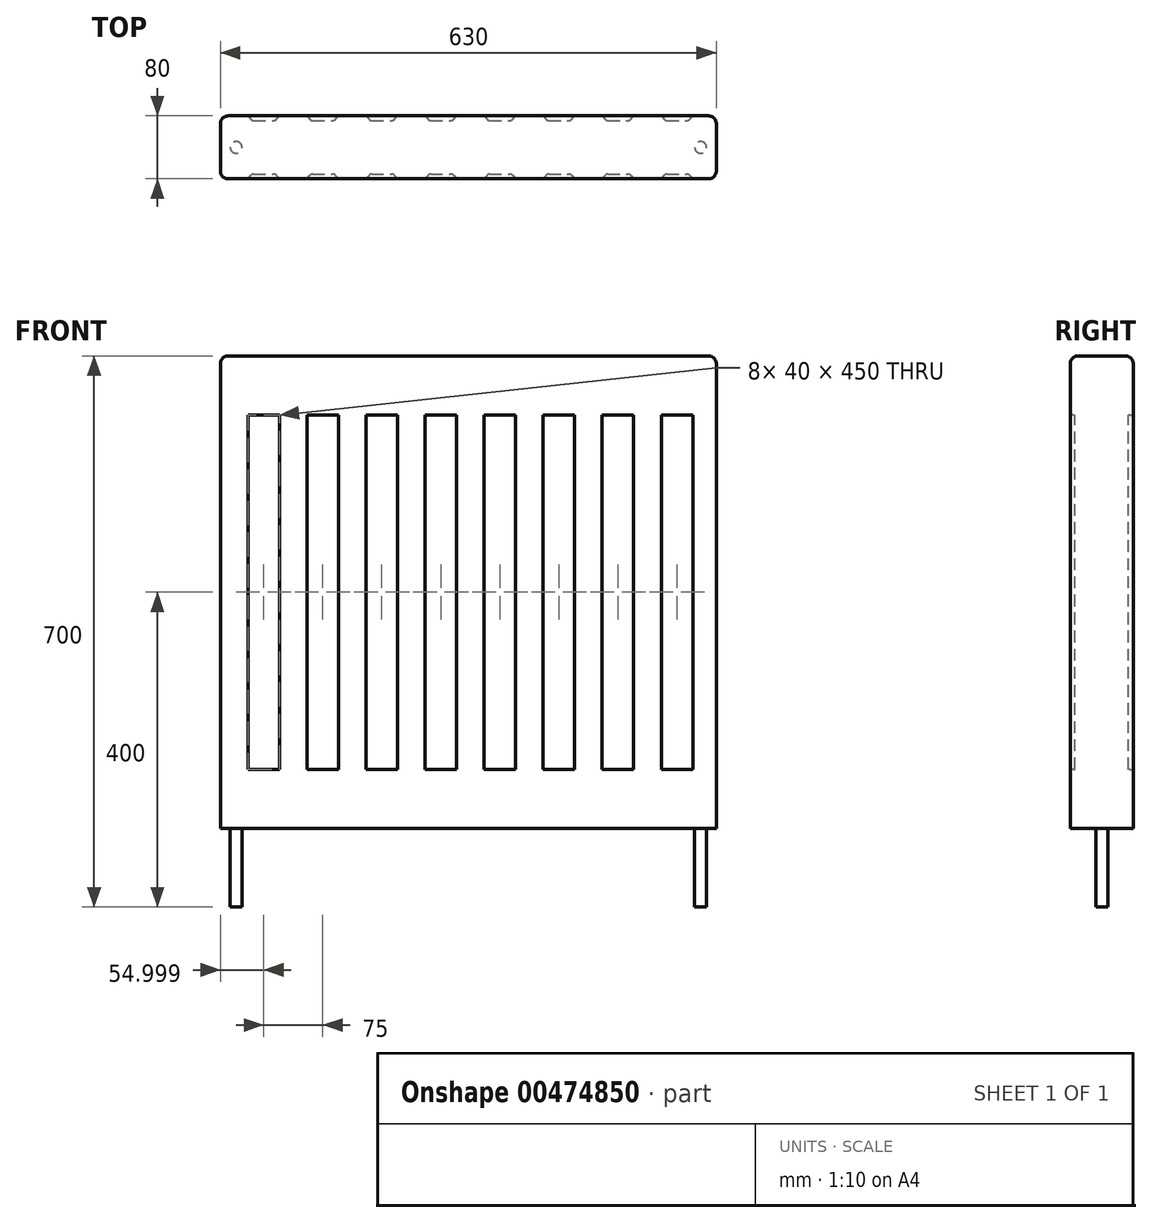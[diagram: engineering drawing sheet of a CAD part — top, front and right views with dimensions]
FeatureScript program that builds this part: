
annotation { "Feature Type Name" : "Feature", "Feature Type Description" : "" }
export const myFeature = defineFeature(function(context is Context, id is Id, definition is map)
    precondition{}
    {
        {
            var Q0;
            Q0=qCreatedBy(makeId("Top.planeOp"),FACE);
            var sketch = newSketch(context, id + "F0", { "sketchPlane" : qUnion([Q0])});
            skLineSegment(sketch, "E0.bottom", {"start": v(-345.66, -18.68) * mm, "end": v(284.34, -18.68) * mm});
            skLineSegment(sketch, "E0.top", {"start": v(-345.66, -98.68) * mm, "end": v(284.34, -98.68) * mm});
            skLineSegment(sketch, "E0.left", {"start": v(-345.66, -18.68) * mm, "end": v(-345.66, -98.68) * mm});
            skLineSegment(sketch, "E0.right", {"start": v(284.34, -18.68) * mm, "end": v(284.34, -98.68) * mm});
            skSolve(sketch);
        }
        {
            var Q0;
            Q0=makeQuery(id+"F0.imprint","IMPRINT",FACE,{"disambiguationData":[TD([[makeQuery(id+"F0.imprint","IMPRINT",EDGE,{"derivedFrom":sQuery(id+"F0.wireOp",EDGE,"E0.bottom")}),-1.0]])]});
            extrude(context, id + "F1", {"entities" : qUnion([Q0]), "endBound" : BoundingType.SYMMETRIC, "depth" : 600 * mm});
        }
        {
            var Q0;
            Q0=makeQuery(id+"F1.opExtrude","CAP_FACE",FACE,{"disambiguationData":[OSD([sQuery(id+"F0.wireOp",EDGE,"E0.bottom"),sQuery(id+"F0.wireOp",EDGE,"E0.top"),sQuery(id+"F0.wireOp",EDGE,"E0.left"),sQuery(id+"F0.wireOp",EDGE,"E0.right")])],"isStart":true});
            var sketch = newSketch(context, id + "F2", { "sketchPlane" : qUnion([Q0])});
            skCircle(sketch, "E1", {"center": v(-325.66, 58.68) * mm, "radius": 7.5 * mm});
            skPoint(sketch, "E1.centerSnap0", {"position": v(-345.66, 58.68) * mm});
            skCircle(sketch, "E2", {"center": v(264.34, 58.68) * mm, "radius": 7.5 * mm});
            skPoint(sketch, "E2.centerSnap0", {"position": v(284.34, 58.68) * mm});
            skSolve(sketch);
        }
        {
            var Q0;
            Q0=makeQuery(id+"F2.imprint","IMPRINT",FACE,{"disambiguationData":[TD([[makeQuery(id+"F2.imprint","IMPRINT",EDGE,{"derivedFrom":sQuery(id+"F2.wireOp",EDGE,"E2")}),1.0]])]});
            var Q1;
            Q1=makeQuery(id+"F2.imprint","IMPRINT",FACE,{"disambiguationData":[TD([[makeQuery(id+"F2.imprint","IMPRINT",EDGE,{"derivedFrom":sQuery(id+"F2.wireOp",EDGE,"E1")}),1.0]])]});
            extrude(context, id + "F3", {"entities" : qUnion([Q0, Q1]), "operationType" : NewBodyOperationType.ADD, "depth" : 100 * mm});
        }
        {
            var Q0;
            Q0=qCreatedBy(makeId("Top.planeOp"),FACE);
            var sketch = newSketch(context, id + "F4", { "sketchPlane" : qUnion([Q0])});
            skLineSegment(sketch, "E3", {"start": v(-310.66, -18.68) * mm, "end": v(-307.12, -22.9) * mm});
            skLineSegment(sketch, "E4", {"start": v(-303.3, -24.68) * mm, "end": v(-278.03, -24.68) * mm});
            skLineSegment(sketch, "E5", {"start": v(-274.2, -22.9) * mm, "end": v(-270.66, -18.68) * mm});
            skPoint(sketch, "E6.visualSharp", {"position": v(-305.63, -24.68) * mm});
            skArc(sketch, "E6.filletArc", {"start": v(-307.12, -22.9) * mm, "mid": v(-305.4, -24.22) * mm, "end": v(-303.3, -24.68) * mm});
            skPoint(sketch, "E7.visualSharp", {"position": v(-275.7, -24.68) * mm});
            skArc(sketch, "E7.filletArc", {"start": v(-278.03, -24.68) * mm, "mid": v(-275.91, -24.22) * mm, "end": v(-274.2, -22.9) * mm});
            skLineSegment(sketch, "E8.1.0.0", {"start": v(-235.66, -18.68) * mm, "end": v(-232.12, -22.9) * mm});
            skArc(sketch, "E8.1.0.1", {"start": v(-232.12, -22.9) * mm, "mid": v(-230.4, -24.22) * mm, "end": v(-228.3, -24.68) * mm});
            skLineSegment(sketch, "E8.1.0.2", {"start": v(-228.3, -24.68) * mm, "end": v(-203.03, -24.68) * mm});
            skArc(sketch, "E8.1.0.3", {"start": v(-203.03, -24.68) * mm, "mid": v(-200.91, -24.22) * mm, "end": v(-199.2, -22.9) * mm});
            skLineSegment(sketch, "E8.1.0.4", {"start": v(-199.2, -22.9) * mm, "end": v(-195.66, -18.68) * mm});
            skLineSegment(sketch, "E8.2.0.0", {"start": v(-160.66, -18.68) * mm, "end": v(-157.12, -22.9) * mm});
            skArc(sketch, "E8.2.0.1", {"start": v(-157.12, -22.9) * mm, "mid": v(-155.4, -24.22) * mm, "end": v(-153.3, -24.68) * mm});
            skLineSegment(sketch, "E8.2.0.2", {"start": v(-153.3, -24.68) * mm, "end": v(-128.03, -24.68) * mm});
            skArc(sketch, "E8.2.0.3", {"start": v(-128.03, -24.68) * mm, "mid": v(-125.91, -24.22) * mm, "end": v(-124.2, -22.9) * mm});
            skLineSegment(sketch, "E8.2.0.4", {"start": v(-124.2, -22.9) * mm, "end": v(-120.66, -18.68) * mm});
            skLineSegment(sketch, "E8.3.0.0", {"start": v(-85.66, -18.68) * mm, "end": v(-82.12, -22.9) * mm});
            skArc(sketch, "E8.3.0.1", {"start": v(-82.12, -22.9) * mm, "mid": v(-80.4, -24.22) * mm, "end": v(-78.3, -24.68) * mm});
            skLineSegment(sketch, "E8.3.0.2", {"start": v(-78.3, -24.68) * mm, "end": v(-53.03, -24.68) * mm});
            skArc(sketch, "E8.3.0.3", {"start": v(-53.03, -24.68) * mm, "mid": v(-50.91, -24.22) * mm, "end": v(-49.2, -22.9) * mm});
            skLineSegment(sketch, "E8.3.0.4", {"start": v(-49.2, -22.9) * mm, "end": v(-45.66, -18.68) * mm});
            skLineSegment(sketch, "E8.4.0.0", {"start": v(-10.66, -18.68) * mm, "end": v(-7.12, -22.9) * mm});
            skArc(sketch, "E8.4.0.1", {"start": v(-7.12, -22.9) * mm, "mid": v(-5.4, -24.22) * mm, "end": v(-3.3, -24.68) * mm});
            skLineSegment(sketch, "E8.4.0.2", {"start": v(-3.3, -24.68) * mm, "end": v(21.97, -24.68) * mm});
            skArc(sketch, "E8.4.0.3", {"start": v(21.97, -24.68) * mm, "mid": v(24.09, -24.22) * mm, "end": v(25.8, -22.9) * mm});
            skLineSegment(sketch, "E8.4.0.4", {"start": v(25.8, -22.9) * mm, "end": v(29.34, -18.68) * mm});
            skLineSegment(sketch, "E8.5.0.0", {"start": v(64.34, -18.68) * mm, "end": v(67.88, -22.9) * mm});
            skArc(sketch, "E8.5.0.1", {"start": v(67.88, -22.9) * mm, "mid": v(69.6, -24.22) * mm, "end": v(71.7, -24.68) * mm});
            skLineSegment(sketch, "E8.5.0.2", {"start": v(71.7, -24.68) * mm, "end": v(96.97, -24.68) * mm});
            skArc(sketch, "E8.5.0.3", {"start": v(96.97, -24.68) * mm, "mid": v(99.09, -24.22) * mm, "end": v(100.8, -22.9) * mm});
            skLineSegment(sketch, "E8.5.0.4", {"start": v(100.8, -22.9) * mm, "end": v(104.34, -18.68) * mm});
            skLineSegment(sketch, "E8.6.0.0", {"start": v(139.34, -18.68) * mm, "end": v(142.88, -22.9) * mm});
            skArc(sketch, "E8.6.0.1", {"start": v(142.88, -22.9) * mm, "mid": v(144.6, -24.22) * mm, "end": v(146.7, -24.68) * mm});
            skLineSegment(sketch, "E8.6.0.2", {"start": v(146.7, -24.68) * mm, "end": v(171.97, -24.68) * mm});
            skArc(sketch, "E8.6.0.3", {"start": v(171.97, -24.68) * mm, "mid": v(174.09, -24.22) * mm, "end": v(175.8, -22.9) * mm});
            skLineSegment(sketch, "E8.6.0.4", {"start": v(175.8, -22.9) * mm, "end": v(179.34, -18.68) * mm});
            skLineSegment(sketch, "E8.7.0.0", {"start": v(214.34, -18.68) * mm, "end": v(217.88, -22.9) * mm});
            skArc(sketch, "E8.7.0.1", {"start": v(217.88, -22.9) * mm, "mid": v(219.6, -24.22) * mm, "end": v(221.7, -24.68) * mm});
            skLineSegment(sketch, "E8.7.0.2", {"start": v(221.7, -24.68) * mm, "end": v(246.97, -24.68) * mm});
            skArc(sketch, "E8.7.0.3", {"start": v(246.97, -24.68) * mm, "mid": v(249.09, -24.22) * mm, "end": v(250.8, -22.9) * mm});
            skLineSegment(sketch, "E8.7.0.4", {"start": v(250.8, -22.9) * mm, "end": v(254.34, -18.68) * mm});
            skLineSegment(sketch, "E9", {"start": v(-345.66, -58.68) * mm, "end": v(284.34, -58.68) * mm, "construction": true});
            skArc(sketch, "E10.MirrorCS", {"start": v(-307.12, -94.47) * mm, "mid": v(-305.4, -93.15) * mm, "end": v(-303.3, -92.68) * mm});
            skLineSegment(sketch, "E11.MirrorCS", {"start": v(-310.66, -98.68) * mm, "end": v(-307.12, -94.47) * mm});
            skLineSegment(sketch, "E12.MirrorCS", {"start": v(-274.2, -94.47) * mm, "end": v(-270.66, -98.68) * mm});
            skLineSegment(sketch, "E13.MirrorCS", {"start": v(-235.66, -98.68) * mm, "end": v(-232.12, -94.47) * mm});
            skArc(sketch, "E14.MirrorCS", {"start": v(-278.03, -92.68) * mm, "mid": v(-275.91, -93.15) * mm, "end": v(-274.2, -94.47) * mm});
            skArc(sketch, "E15.MirrorCS", {"start": v(-232.12, -94.47) * mm, "mid": v(-230.4, -93.15) * mm, "end": v(-228.3, -92.68) * mm});
            skArc(sketch, "E16.MirrorCS", {"start": v(246.97, -92.68) * mm, "mid": v(249.09, -93.15) * mm, "end": v(250.8, -94.47) * mm});
            skLineSegment(sketch, "E17.MirrorCS", {"start": v(-85.66, -98.68) * mm, "end": v(-82.12, -94.47) * mm});
            skLineSegment(sketch, "E18.MirrorCS", {"start": v(-124.2, -94.47) * mm, "end": v(-120.66, -98.68) * mm});
            skArc(sketch, "E19.MirrorCS", {"start": v(-128.03, -92.68) * mm, "mid": v(-125.91, -93.15) * mm, "end": v(-124.2, -94.47) * mm});
            skLineSegment(sketch, "E20.MirrorCS", {"start": v(-10.66, -98.68) * mm, "end": v(-7.12, -94.47) * mm});
            skArc(sketch, "E21.MirrorCS", {"start": v(217.88, -94.47) * mm, "mid": v(219.6, -93.15) * mm, "end": v(221.7, -92.68) * mm});
            skLineSegment(sketch, "E22.MirrorCS", {"start": v(100.8, -94.47) * mm, "end": v(104.34, -98.68) * mm});
            skArc(sketch, "E23.MirrorCS", {"start": v(-7.12, -94.47) * mm, "mid": v(-5.4, -93.15) * mm, "end": v(-3.3, -92.68) * mm});
            skLineSegment(sketch, "E24.MirrorCS", {"start": v(139.34, -98.68) * mm, "end": v(142.88, -94.47) * mm});
            skLineSegment(sketch, "E25.MirrorCS", {"start": v(-49.2, -94.47) * mm, "end": v(-45.66, -98.68) * mm});
            skLineSegment(sketch, "E26.MirrorCS", {"start": v(214.34, -98.68) * mm, "end": v(217.88, -94.47) * mm});
            skArc(sketch, "E27.MirrorCS", {"start": v(67.88, -94.47) * mm, "mid": v(69.6, -93.15) * mm, "end": v(71.7, -92.68) * mm});
            skArc(sketch, "E28.MirrorCS", {"start": v(-53.03, -92.68) * mm, "mid": v(-50.91, -93.15) * mm, "end": v(-49.2, -94.47) * mm});
            skLineSegment(sketch, "E29.MirrorCS", {"start": v(175.8, -94.47) * mm, "end": v(179.34, -98.68) * mm});
            skLineSegment(sketch, "E30.MirrorCS", {"start": v(64.34, -98.68) * mm, "end": v(67.88, -94.47) * mm});
            skArc(sketch, "E31.MirrorCS", {"start": v(-157.12, -94.47) * mm, "mid": v(-155.4, -93.15) * mm, "end": v(-153.3, -92.68) * mm});
            skArc(sketch, "E32.MirrorCS", {"start": v(96.97, -92.68) * mm, "mid": v(99.09, -93.15) * mm, "end": v(100.8, -94.47) * mm});
            skArc(sketch, "E33.MirrorCS", {"start": v(171.97, -92.68) * mm, "mid": v(174.09, -93.15) * mm, "end": v(175.8, -94.47) * mm});
            skLineSegment(sketch, "E34.MirrorCS", {"start": v(25.8, -94.47) * mm, "end": v(29.34, -98.68) * mm});
            skLineSegment(sketch, "E35.MirrorCS", {"start": v(-160.66, -98.68) * mm, "end": v(-157.12, -94.47) * mm});
            skLineSegment(sketch, "E36.MirrorCS", {"start": v(-199.2, -94.47) * mm, "end": v(-195.66, -98.68) * mm});
            skArc(sketch, "E37.MirrorCS", {"start": v(-203.03, -92.68) * mm, "mid": v(-200.91, -93.15) * mm, "end": v(-199.2, -94.47) * mm});
            skArc(sketch, "E38.MirrorCS", {"start": v(21.97, -92.68) * mm, "mid": v(24.09, -93.15) * mm, "end": v(25.8, -94.47) * mm});
            skLineSegment(sketch, "E39.MirrorCS", {"start": v(250.8, -94.47) * mm, "end": v(254.34, -98.68) * mm});
            skArc(sketch, "E40.MirrorCS", {"start": v(142.88, -94.47) * mm, "mid": v(144.6, -93.15) * mm, "end": v(146.7, -92.68) * mm});
            skArc(sketch, "E41.MirrorCS", {"start": v(-82.12, -94.47) * mm, "mid": v(-80.4, -93.15) * mm, "end": v(-78.3, -92.68) * mm});
            skLineSegment(sketch, "E42.MirrorCS", {"start": v(-303.3, -92.68) * mm, "end": v(-278.03, -92.68) * mm});
            skLineSegment(sketch, "E43.MirrorCS", {"start": v(-3.3, -92.68) * mm, "end": v(21.97, -92.68) * mm});
            skLineSegment(sketch, "E44.MirrorCS", {"start": v(146.7, -92.68) * mm, "end": v(171.97, -92.68) * mm});
            skLineSegment(sketch, "E45.MirrorCS", {"start": v(71.7, -92.68) * mm, "end": v(96.97, -92.68) * mm});
            skLineSegment(sketch, "E46.MirrorCS", {"start": v(221.7, -92.68) * mm, "end": v(246.97, -92.68) * mm});
            skPoint(sketch, "E47.MirrorP", {"position": v(-275.7, -92.68) * mm});
            skLineSegment(sketch, "E48.MirrorCS", {"start": v(-153.3, -92.68) * mm, "end": v(-128.03, -92.68) * mm});
            skLineSegment(sketch, "E49.MirrorCS", {"start": v(-78.3, -92.68) * mm, "end": v(-53.03, -92.68) * mm});
            skPoint(sketch, "E50.MirrorP", {"position": v(-305.63, -92.68) * mm});
            skLineSegment(sketch, "E51.MirrorCS", {"start": v(-228.3, -92.68) * mm, "end": v(-203.03, -92.68) * mm});
            skLineSegment(sketch, "E52", {"start": v(-310.66, -18.68) * mm, "end": v(-270.66, -18.68) * mm});
            skLineSegment(sketch, "E53", {"start": v(-235.66, -18.68) * mm, "end": v(-195.66, -18.68) * mm});
            skLineSegment(sketch, "E54", {"start": v(-160.66, -18.68) * mm, "end": v(-120.66, -18.68) * mm});
            skLineSegment(sketch, "E55", {"start": v(-85.66, -18.68) * mm, "end": v(-45.66, -18.68) * mm});
            skLineSegment(sketch, "E56", {"start": v(-10.66, -18.68) * mm, "end": v(29.34, -18.68) * mm});
            skLineSegment(sketch, "E57", {"start": v(64.34, -18.68) * mm, "end": v(104.34, -18.68) * mm});
            skLineSegment(sketch, "E58", {"start": v(139.34, -18.68) * mm, "end": v(179.34, -18.68) * mm});
            skLineSegment(sketch, "E59", {"start": v(214.34, -18.68) * mm, "end": v(254.34, -18.68) * mm});
            skLineSegment(sketch, "E60", {"start": v(254.34, -98.68) * mm, "end": v(214.34, -98.68) * mm});
            skLineSegment(sketch, "E61", {"start": v(179.34, -98.68) * mm, "end": v(139.34, -98.68) * mm});
            skLineSegment(sketch, "E62", {"start": v(104.34, -98.68) * mm, "end": v(64.34, -98.68) * mm});
            skLineSegment(sketch, "E63", {"start": v(29.34, -98.68) * mm, "end": v(-10.66, -98.68) * mm});
            skLineSegment(sketch, "E64", {"start": v(-45.66, -98.68) * mm, "end": v(-85.66, -98.68) * mm});
            skLineSegment(sketch, "E65", {"start": v(-120.66, -98.68) * mm, "end": v(-160.66, -98.68) * mm});
            skLineSegment(sketch, "E66", {"start": v(-195.66, -98.68) * mm, "end": v(-235.66, -98.68) * mm});
            skLineSegment(sketch, "E67", {"start": v(-270.66, -98.68) * mm, "end": v(-310.66, -98.68) * mm});
            skSolve(sketch);
        }
        {
            var Q0;
            Q0=qSketchRegion(id+"F4",true);
            extrude(context, id + "F5", {"entities" : qUnion([Q0]), "operationType" : NewBodyOperationType.REMOVE, "endBound" : BoundingType.SYMMETRIC, "oppositeDirection" : true, "depth" : 450 * mm});
        }
        {
            var Q0;
            Q0=makeQuery(id+"F1.opExtrude","SWEPT_EDGE",EDGE,{"disambiguationData":[OSD([sQuery(id+"F0.wireOp",EDGE,"E0.top"),sQuery(id+"F0.wireOp",EDGE,"E0.left")])]});
            var Q1;
            Q1=makeQuery(id+"F1.opExtrude","SWEPT_EDGE",EDGE,{"disambiguationData":[OSD([sQuery(id+"F0.wireOp",EDGE,"E0.bottom"),sQuery(id+"F0.wireOp",EDGE,"E0.left")])]});
            var Q2;
            Q2=makeQuery(id+"F1.opExtrude","SWEPT_EDGE",EDGE,{"disambiguationData":[OSD([sQuery(id+"F0.wireOp",EDGE,"E0.top"),sQuery(id+"F0.wireOp",EDGE,"E0.right")])]});
            var Q3;
            Q3=makeQuery(id+"F1.opExtrude","SWEPT_EDGE",EDGE,{"disambiguationData":[OSD([sQuery(id+"F0.wireOp",EDGE,"E0.bottom"),sQuery(id+"F0.wireOp",EDGE,"E0.right")])]});
            var Q4;
            Q4=makeQuery(id+"F1.opExtrude","CAP_EDGE",EDGE,{"disambiguationData":[OSD([sQuery(id+"F0.wireOp",EDGE,"E0.top")])],"isStart":false});
            var Q5;
            Q5=makeQuery(id+"F1.opExtrude","CAP_EDGE",EDGE,{"disambiguationData":[OSD([sQuery(id+"F0.wireOp",EDGE,"E0.bottom")])],"isStart":false});
            var Q6;
            Q6=makeQuery(id+"F1.opExtrude","CAP_EDGE",EDGE,{"disambiguationData":[OSD([sQuery(id+"F0.wireOp",EDGE,"E0.right")])],"isStart":false});
            var Q7;
            Q7=makeQuery(id+"F1.opExtrude","CAP_EDGE",EDGE,{"disambiguationData":[OSD([sQuery(id+"F0.wireOp",EDGE,"E0.left")])],"isStart":false});
            fillet(context, id + "F6", {"entities" : qUnion([Q0, Q1, Q2, Q3, Q4, Q5, Q6, Q7]), "radius" : 10 * mm, "tangentPropagation" : true, "allowEdgeOverflow" : false});
        }
    });
